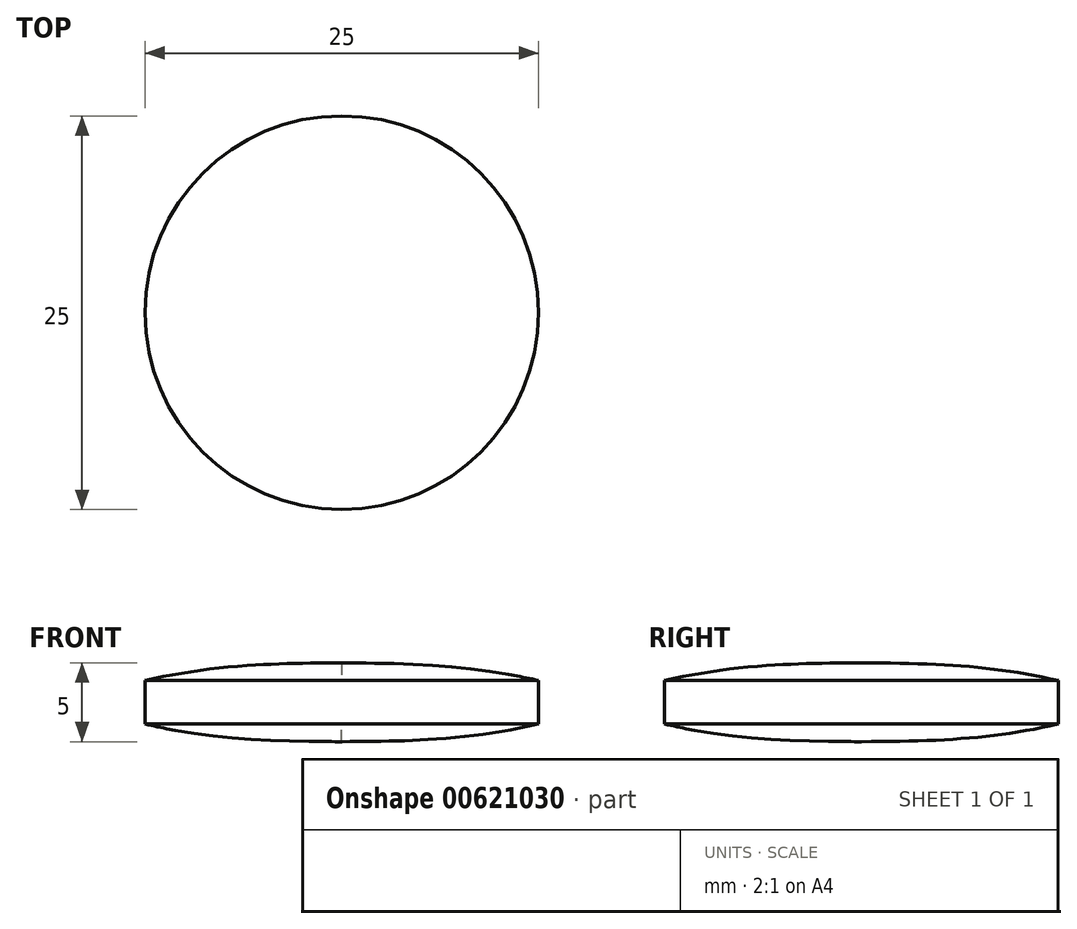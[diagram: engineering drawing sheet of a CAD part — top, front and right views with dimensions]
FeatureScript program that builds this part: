
annotation { "Feature Type Name" : "Feature", "Feature Type Description" : "" }
export const myFeature = defineFeature(function(context is Context, id is Id, definition is map)
    precondition{}
    {
        {
            var Q0;
            Q0=qCreatedBy(makeId("Right.planeOp"),FACE);
            var sketch = newSketch(context, id + "F0", { "sketchPlane" : qUnion([Q0])});
            skLineSegment(sketch, "E0", {"start": v(0, 0) * mm, "end": v(0, 2.5) * mm});
            skLineSegment(sketch, "E1", {"start": v(12.5, 1.38) * mm, "end": v(12.5, 0) * mm});
            skFitSpline(sketch, "E2", {"points": [v(0, 2.5) * mm, v(12.5, 1.38) * mm], "startDerivative": vector(14.7, 0) * mm, "endDerivative": vector(11.87, -2.77) * mm});
            skLineSegment(sketch, "E3.MirrorCS", {"start": v(12.5, -1.38) * mm, "end": v(12.5, 0) * mm});
            skFitSpline(sketch, "E4.MirrorCS", {"points": [v(0, -2.5) * mm, v(12.5, -1.38) * mm], "startDerivative": vector(14.7, 0) * mm, "endDerivative": vector(11.87, 2.77) * mm});
            skLineSegment(sketch, "E5.MirrorCS", {"start": v(0, 0) * mm, "end": v(0, -2.5) * mm});
            skSolve(sketch);
        }
        {
            var Q0;
            Q0=makeQuery(id+"F0.imprint","IMPRINT",FACE,{"disambiguationData":[TD([[makeQuery(id+"F0.imprint","IMPRINT",EDGE,{"derivedFrom":sQuery(id+"F0.wireOp",EDGE,"E0")}),-1.0]])]});
            var Q1;
            Q1=sQuery(id+"F0.wireOp",EDGE,"E0");
            revolve(context, id + "F1", {"entities" : qUnion([Q0]), "axis" : qUnion([Q1]), "revolveType" : RevolveType.FULL});
        }
    });
